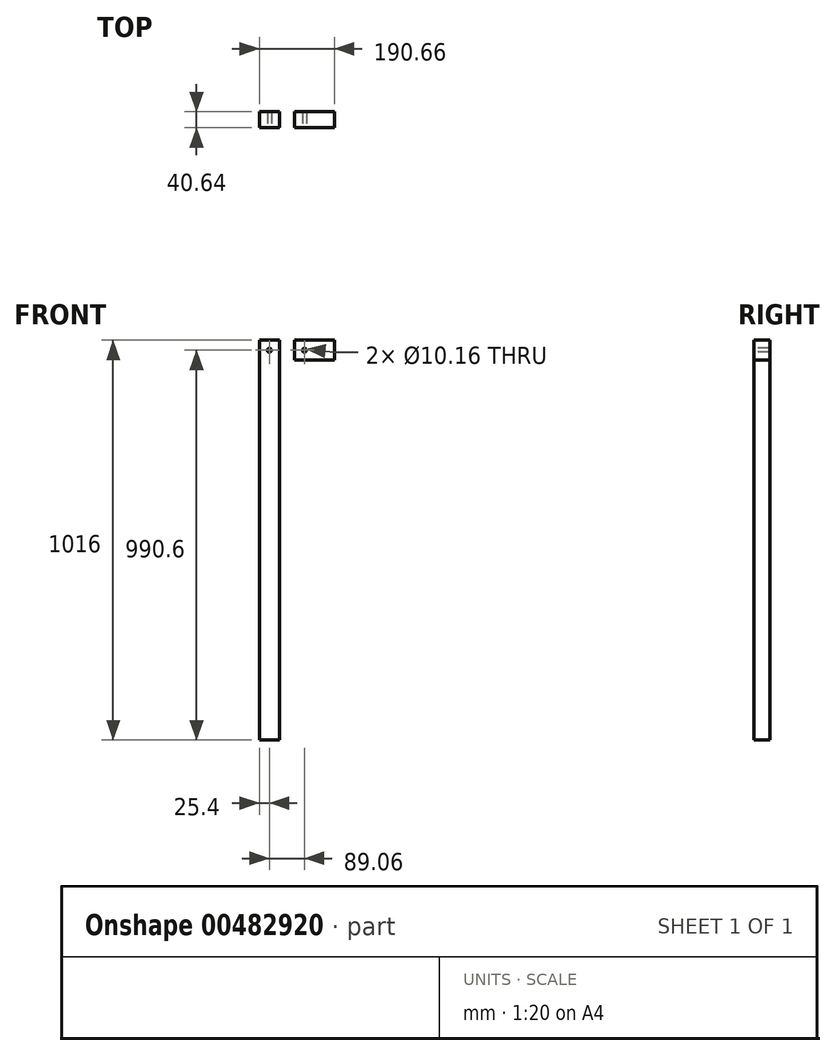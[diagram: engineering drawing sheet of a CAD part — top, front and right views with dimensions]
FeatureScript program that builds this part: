
annotation { "Feature Type Name" : "Feature", "Feature Type Description" : "" }
export const myFeature = defineFeature(function(context is Context, id is Id, definition is map)
    precondition{}
    {
        {
            var Q0;
            Q0=qCreatedBy(makeId("Front.planeOp"),FACE);
            var sketch = newSketch(context, id + "F0", { "sketchPlane" : qUnion([Q0])});
            skLineSegment(sketch, "E0.bottom", {"start": v(25.4, 508) * mm, "end": v(-25.4, 508) * mm});
            skLineSegment(sketch, "E0.top", {"start": v(25.4, -508) * mm, "end": v(-25.4, -508) * mm});
            skLineSegment(sketch, "E0.left", {"start": v(25.4, 508) * mm, "end": v(25.4, -508) * mm});
            skLineSegment(sketch, "E0.right", {"start": v(-25.4, 508) * mm, "end": v(-25.4, -508) * mm});
            skPoint(sketch, "E0.middle", {"position": v(0, 0) * mm});
            skCircle(sketch, "E1", {"center": v(0, 482.6) * mm, "radius": 5.08 * mm});
            skPoint(sketch, "E1.centerSnap0", {"position": v(0, 508) * mm});
            skLineSegment(sketch, "E2.bottom", {"start": v(63.66, 508) * mm, "end": v(165.26, 508) * mm});
            skLineSegment(sketch, "E2.top", {"start": v(63.66, 457.2) * mm, "end": v(165.26, 457.2) * mm});
            skLineSegment(sketch, "E2.left", {"start": v(63.66, 508) * mm, "end": v(63.66, 457.2) * mm});
            skLineSegment(sketch, "E2.right", {"start": v(165.26, 508) * mm, "end": v(165.26, 457.2) * mm});
            skCircle(sketch, "E3", {"center": v(89.06, 482.6) * mm, "radius": 5.08 * mm});
            skSolve(sketch);
        }
        {
            var Q0;
            Q0=makeQuery(id+"F0.imprint","IMPRINT",FACE,{"disambiguationData":[TD([[makeQuery(id+"F0.imprint","IMPRINT",EDGE,{"derivedFrom":sQuery(id+"F0.wireOp",EDGE,"E2.bottom")}),-1.0]])]});
            var Q1;
            Q1=makeQuery(id+"F0.imprint","IMPRINT",FACE,{"disambiguationData":[TD([[makeQuery(id+"F0.imprint","IMPRINT",EDGE,{"derivedFrom":sQuery(id+"F0.wireOp",EDGE,"E0.bottom")}),1.0]])]});
            extrude(context, id + "F1", {"entities" : qUnion([Q0, Q1]), "oppositeDirection" : true, "depth" : 15.24 * mm, "hasSecondDirection" : true, "secondDirectionOppositeDirection" : false, "secondDirectionDepth" : 25.4 * mm});
        }
    });
